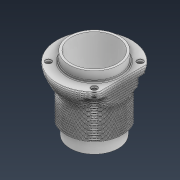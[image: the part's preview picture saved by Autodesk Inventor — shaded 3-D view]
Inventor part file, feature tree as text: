
AUTODESK INVENTOR PART (.ipt)
format: ipt  version: 2022 (Build 260153000, 153)  size: 2,413,568 bytes
history: native  units: mm
features: sketch x17, extrude x15, plane x12, fillet x5, hole x2, pattern_linear x2
ambient origin geometry x8: Origin, YZ Plane, XZ Plane, XY Plane, X Axis, Y Axis, Z Axis, Center Point
bodies: Solid1 (feature_tree)
feature tree (53):
  extrude  "Extrusion1"  Depth=90.0mm
  extrude  "Extrusion2"  Depth=98.0mm
  extrude  "Extrusion3"  Depth=94.0mm
  plane  "Work Plane1"
  extrude  "Extrusion4"  [1 undecoded]
  plane  "Work Plane2"
  extrude  "Extrusion5"  Depth=1.0mm TaperAngle=0.0deg
  plane  "Work Plane3"
  extrude  "Extrusion6"  Depth=139.0mm
  plane  "Work Plane4"
  extrude  "Extrusion7"  Depth=3.0mm
  plane  "Work Plane5"
  extrude  "Extrusion8"  Depth=1.0mm TaperAngle=0.0deg
  plane  "Work Plane6"
  extrude  "Extrusion9"  Depth=135.0mm
  plane  "Work Plane7"
  extrude  "Extrusion10"  Depth=3.0mm
  plane  "Work Plane8"
  extrude  "Extrusion11"  Depth=1.0mm TaperAngle=0.0deg
  plane  "Work Plane9"
  extrude  "Extrusion12"  Depth=128.0mm
  plane  "Work Plane10"
  extrude  "Extrusion13"  Depth=3.0mm
  plane  "Work Plane11"
  extrude  "Extrusion14"  Depth=1.0mm TaperAngle=0.0deg
  sketch  "Sketch15"  dims[d38=3.0mm d39=120.0mm]
  hole  "Hole1"  [1 undecoded]
  pattern_linear  "Rectangular Pattern1"  Spacing1=114.0mm  [1 undecoded]
  hole  "Hole2"  [1 undecoded]
  fillet  "Fillet1"  Radius=3.0mm
  fillet  "Fillet2"  Radius=110.0mm
  pattern_linear  "Rectangular Pattern2"  Spacing1=1.0mm  [1 undecoded]
  plane  "Work Plane12"
  extrude  "Extrusion15"  Depth=3.0mm
  fillet  "Fillet3"  Radius=106.0mm
  fillet  "Fillet4"  Radius=1.0mm
  fillet  "Fillet5"  Radius=121.5mm
  sketch  "Sketch1"  dims[d0=85.5mm d1=90.0mm]
  sketch  "Sketch2"  dims[d2=24.0mm d3=0.0mm d4=98.0mm]
  sketch  "Sketch3"  dims[d5=97.5mm d6=0.0mm d7=94.0mm]
  sketch  "Sketch4"  dims[d8=15.0mm d9=0.0mm d10=-3.0mm]
  sketch  "Sketch5"  dims[d11=140.0mm d12=1.0mm d13=0.0mm]
  sketch  "Sketch6"  dims[d14=3.0mm d15=139.0mm]
  sketch  "Sketch7"  dims[d16=1.0mm d17=0.0mm d18=3.0mm]
  sketch  "Sketch8"  dims[d19=137.0mm d20=1.0mm d21=0.0mm]
  sketch  "Sketch9"  dims[d22=3.0mm d23=135.0mm]
  sketch  "Sketch10"  dims[d24=1.0mm d25=0.0mm d26=3.0mm]
  sketch  "Sketch11"  dims[d27=132.0mm d28=1.0mm d29=0.0mm]
  sketch  "Sketch12"  dims[d30=3.0mm d31=128.0mm]
  sketch  "Sketch13"  dims[d32=1.0mm d33=0.0mm d34=3.0mm]
  sketch  "Sketch14"  dims[d35=124.0mm d36=1.0mm d37=0.0mm]
  sketch  "Sketch16"  dims[d40=1.0mm d41=0.0mm]
  sketch  "Sketch17"  dims[d42=3.0mm d43=114.0mm d44=1.0mm d45=0.0mm d46=3.0mm d47=110.0mm d48=1.0mm d49=0.0mm d50=3.0mm d51=106.0mm d52=1.0mm d53=0.0mm d54=121.5mm d55=45.0deg d56=40.0mm d58=360.0deg d60=11.5mm d61=6.0mm d62=4.0mm d63=2.0mm d64=90.0deg d65=12.4mm d66=20.594885mm d67=20.0mm d68=6.0mm d69=4.0mm d70=2.0mm d71=90.0deg d72=8.0mm d73=20.594885mm d74=10.0mm d75=140.0mm d77=-4.0mm d78=10.0mm d79=140.0mm d81=4.0mm d82=-80.0mm d83=16.0mm d84=1.0mm d85=0.0mm d86=8.0mm d87=1.5mm d88=0.5mm]
note: 5 required parameter values undecoded (feature->parameter linkage not recoverable at this tier; creation-order binding heuristic only, values carry confidence <= 0.55)
